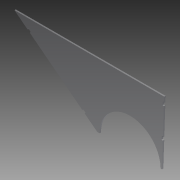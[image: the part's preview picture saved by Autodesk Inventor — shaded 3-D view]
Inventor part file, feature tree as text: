
AUTODESK INVENTOR PART (.ipt)
format: ipt  version: 2013 (Build 170138000, 138)  size: 122,880 bytes
history: native  units: in
note: dims shown in document units (in); Inventor stores cm internally (conversion verified against a paired STEP export)
features: extrude x3, sketch x3
ambient origin geometry x8: Origin, YZ Plane, XZ Plane, XY Plane, X Axis, Y Axis, Z Axis, Center Point
bodies: Solid1 (feature_tree)
feature tree (6):
  extrude  "Extrusion1"  Depth=1.4in
  extrude  "Extrusion2"  Depth=27.0in
  extrude  "Extrusion3"  Depth=0.25in
  sketch  "Sketch1"  dims[d2=11.547in d3=1.4in]
  sketch  "Sketch2"  dims[d4=1.0in d5=27.0in]
  sketch  "Sketch3"  dims[d8=11.0in d11=0.25in d12=0.25in d13=0.25in d14=0.0in d21=0.5in d23=0.5in d24=1.0in d25=5.0in d26=0.25in d27=0.0in d28=0.25in d29=0.5in d30=0.5in d31=3.0in d32=12.0in d33=0.25in d34=0.0in]
